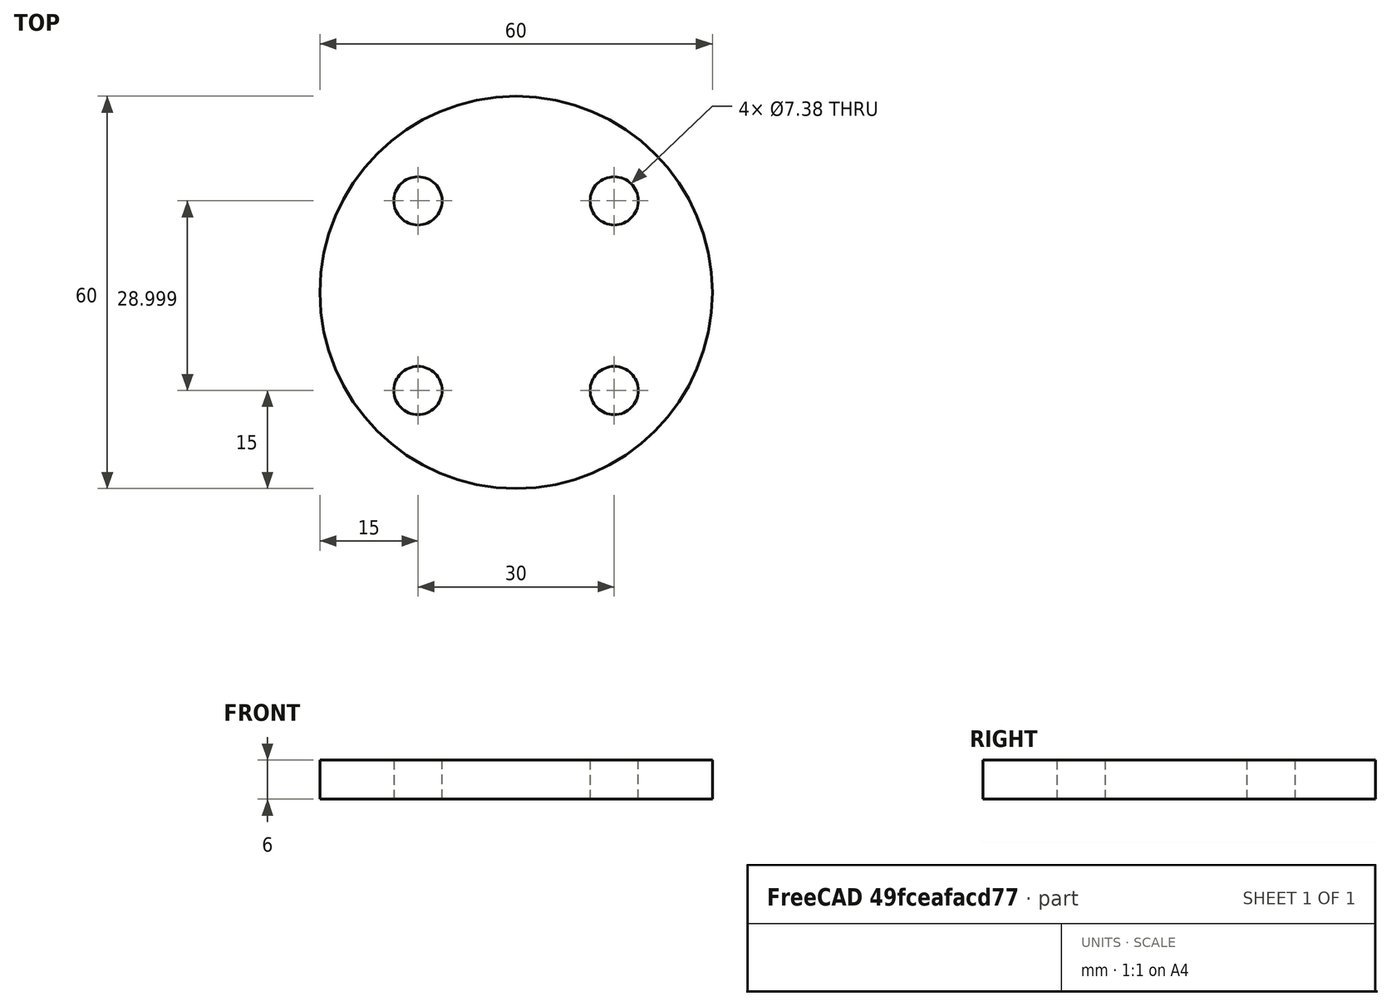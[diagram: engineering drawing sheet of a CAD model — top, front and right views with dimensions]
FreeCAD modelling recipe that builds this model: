
FCSTD DOCUMENT  (FreeCAD 0.21R33694 (Git))
Label: OJT1_T019_R03_tamboret_rodo
License: All rights reserved
LicenseURL: http://en.wikipedia.org/wiki/All_rights_reserved
objects: Sketcher::SketchObject×1, PartDesign::Pad×1, PartDesign::Body×1
note: 4 computed .brp shape members not serialized (recipe doc carries the construction recipe); baked Part::Feature solids carry a one-line shape summary decoded from their .brp

FEATURE [Sketcher::SketchObject] Sketch
  FullyConstrained = false
  MapMode = 5
  Support = -> [XY_Plane]
  sketch-geometry (9):
    g0: Circle CenterX=0 CenterY=0 CenterZ=0 NormalX=0 NormalY=0 NormalZ=1 AngleXU=0 Radius=30
    g1: Circle CenterX=14.9977 CenterY=13.9992 CenterZ=0 NormalX=0 NormalY=0 NormalZ=1 AngleXU=0 Radius=3.68763
    g2: Circle CenterX=-14.9977 CenterY=13.9992 CenterZ=0 NormalX=0 NormalY=0 NormalZ=1 AngleXU=0 Radius=3.68763
    g3: Circle CenterX=15 CenterY=-15 CenterZ=0 NormalX=0 NormalY=0 NormalZ=1 AngleXU=0 Radius=3.68763
    g4: Circle CenterX=-15 CenterY=-15 CenterZ=0 NormalX=0 NormalY=0 NormalZ=1 AngleXU=0 Radius=3.68763
    g5: LineSegment StartX=-14.9958 StartY=17.0684 StartZ=0 EndX=-14.9958 EndY=-17.6574 EndZ=0
    g6: LineSegment StartX=15 StartY=18.0177 StartZ=0 EndX=15 EndY=-20.5947 EndZ=0
    g7: LineSegment StartX=-21.2698 StartY=-15 StartZ=0 EndX=23.1449 EndY=-15 EndZ=0
    g8: LineSegment StartX=-21.5318 StartY=15.1529 StartZ=0 EndX=23.7453 EndY=15.1529 EndZ=0
  constraints (10):
    c: Tangent(g0,g-1) = -1.5708
    c: Symmetric(g1,g2,g-2)
    c: Symmetric(g4,g3,g-2)
    c: Equal(g1,g2)
    c: Equal(g2,g4)
    c: Equal(g3,g4)
    c: Vertical(g5)
    c: Vertical(g6)
    c: Horizontal(g7)
    c: Horizontal(g8)
FEATURE [PartDesign::Pad] Pad
  Direction = (0,0,1)
  Length = 6
  Length2 = 10
  Profile = -> Sketch
  ReferenceAxis = -> Sketch [N_Axis]
  Type = 0
FEATURE [PartDesign::Body] Body
  Group = -> [Sketch,Pad]
  Origin = -> Origin
  Tip = -> Pad
